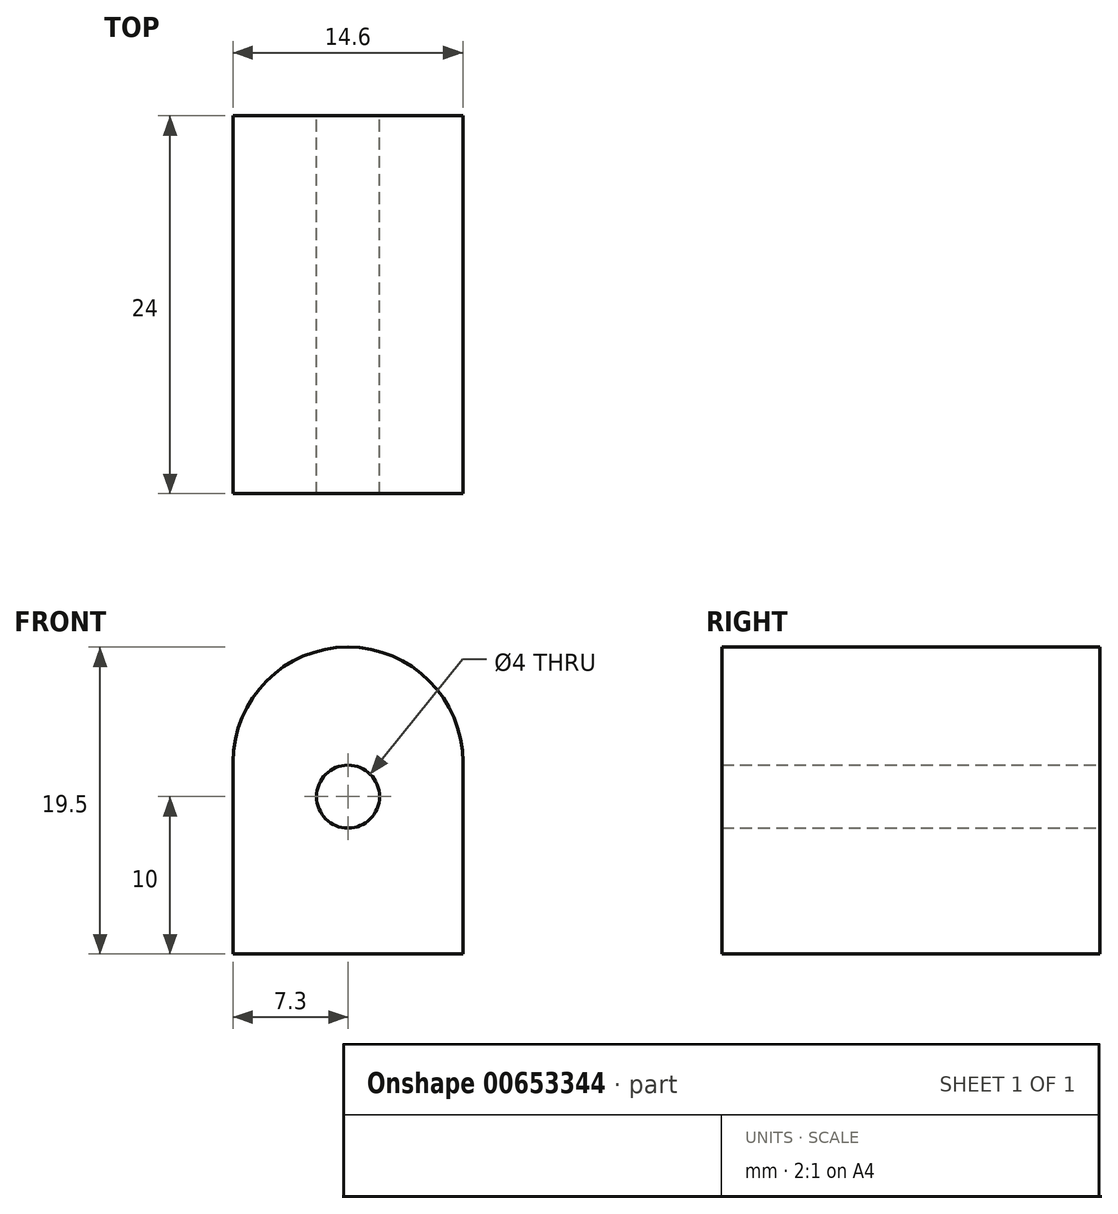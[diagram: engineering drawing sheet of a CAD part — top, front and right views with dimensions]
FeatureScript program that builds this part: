
annotation { "Feature Type Name" : "Feature", "Feature Type Description" : "" }
export const myFeature = defineFeature(function(context is Context, id is Id, definition is map)
    precondition{}
    {
        {
            var Q0;
            Q0=qCreatedBy(makeId("Front.planeOp"),FACE);
            var sketch = newSketch(context, id + "F0", { "sketchPlane" : qUnion([Q0])});
            skLineSegment(sketch, "E0.top", {"start": v(-7.3, -9.75) * mm, "end": v(7.3, -9.75) * mm});
            skLineSegment(sketch, "E0.left", {"start": v(-7.3, 2.45) * mm, "end": v(-7.3, -9.75) * mm});
            skLineSegment(sketch, "E0.right", {"start": v(7.3, 2.45) * mm, "end": v(7.3, -9.75) * mm});
            skPoint(sketch, "E0.middle", {"position": v(0, 0) * mm});
            skArc(sketch, "E1", {"start": v(7.3, 2.45) * mm, "mid": v(0, 9.75) * mm, "end": v(-7.3, 2.45) * mm});
            skPoint(sketch, "E1.centerSnap0", {"position": v(0, 9.75) * mm});
            skPoint(sketch, "E2.orphan", {"position": v(-7.3, 9.75) * mm});
            skPoint(sketch, "E3.orphan", {"position": v(7.3, 9.75) * mm});
            skCircle(sketch, "E4", {"center": v(0, 0.25) * mm, "radius": 2 * mm});
            skSolve(sketch);
        }
        {
            var Q0;
            Q0=qSketchRegion(id+"F0",true);
            extrude(context, id + "F1", {"entities" : qUnion([Q0]), "depth" : 24 * mm, "offsetDistance" : 25 * mm});
        }
    });
